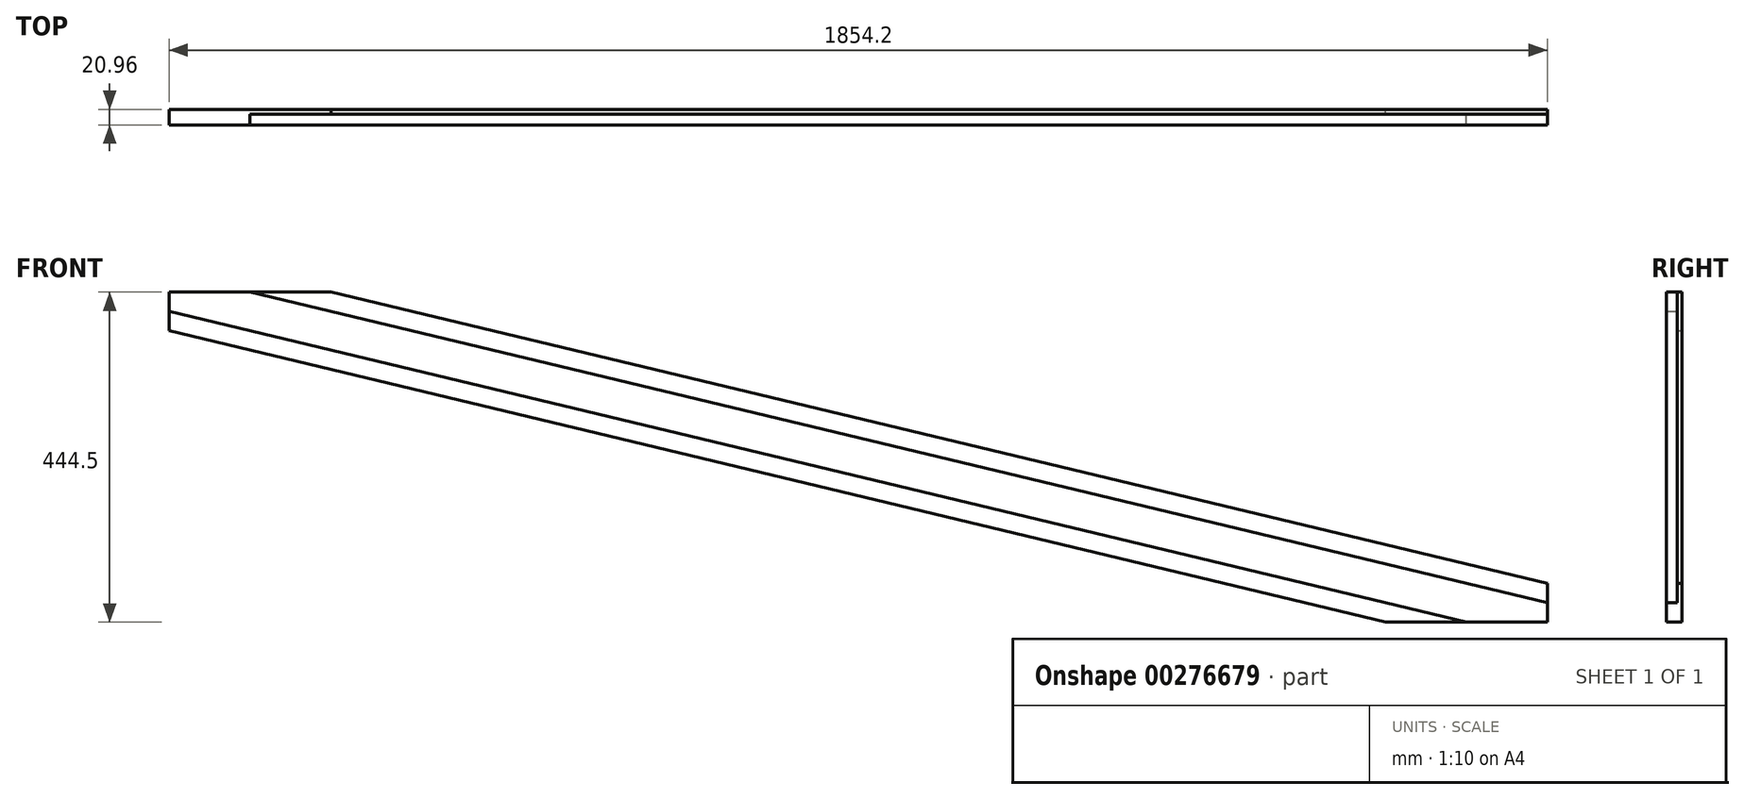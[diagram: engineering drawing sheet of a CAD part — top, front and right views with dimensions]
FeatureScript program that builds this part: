
annotation { "Feature Type Name" : "Feature", "Feature Type Description" : "" }
export const myFeature = defineFeature(function(context is Context, id is Id, definition is map)
    precondition{}
    {
        {
            var Q0;
            Q0=qCreatedBy(makeId("Front.planeOp"),FACE);
            var sketch = newSketch(context, id + "F0", { "sketchPlane" : qUnion([Q0])});
            skLineSegment(sketch, "E0.bottom", {"start": v(1636.29, 0) * mm, "end": v(1854.2, 0) * mm});
            skLineSegment(sketch, "E0.top", {"start": v(0, 444.5) * mm, "end": v(217.91, 444.5) * mm});
            skLineSegment(sketch, "E0.left", {"start": v(0, 392.26) * mm, "end": v(0, 444.5) * mm});
            skLineSegment(sketch, "E0.right", {"start": v(1854.2, 0) * mm, "end": v(1854.2, 52.24) * mm});
            skLineSegment(sketch, "E1", {"start": v(0, 444.5) * mm, "end": v(1854.2, 0) * mm});
            skLineSegment(sketch, "E2.0", {"start": v(0, 418.38) * mm, "end": v(1745.24, 0) * mm});
            skLineSegment(sketch, "E3.0", {"start": v(108.96, 444.5) * mm, "end": v(1854.2, 26.12) * mm});
            skLineSegment(sketch, "E4.0", {"start": v(0, 392.26) * mm, "end": v(1636.29, 0) * mm});
            skLineSegment(sketch, "E5.0", {"start": v(217.91, 444.5) * mm, "end": v(1854.2, 52.24) * mm});
            skSolve(sketch);
        }
        {
            var Q0;
            {var subQ0=sQuery(id+"F0.wireOp",EDGE,"E1");Q0=makeQuery(id+"F0.imprint","IMPRINT",FACE,{"disambiguationData":[TD([[makeQuery(id+"F0.imprint","IMPRINT",EDGE,{"derivedFrom":subQ0}),-1.0]])]});}
            var Q1;
            {var subQ0=sQuery(id+"F0.wireOp",EDGE,"E1");Q1=makeQuery(id+"F0.imprint","IMPRINT",FACE,{"disambiguationData":[TD([[makeQuery(id+"F0.imprint","IMPRINT",EDGE,{"derivedFrom":subQ0}),1.0]])]});}
            extrude(context, id + "F1", {"entities" : qUnion([Q0, Q1]), "depth" : 20.95 * mm});
        }
        {
            var Q0;
            Q0 = qSketchRegion(id + "F0", true);
            extrude(context, id + "F2", {"entities" : qUnion([Q0]), "operationType" : NewBodyOperationType.ADD, "depth" : 6.35 * mm});
        }
    });
